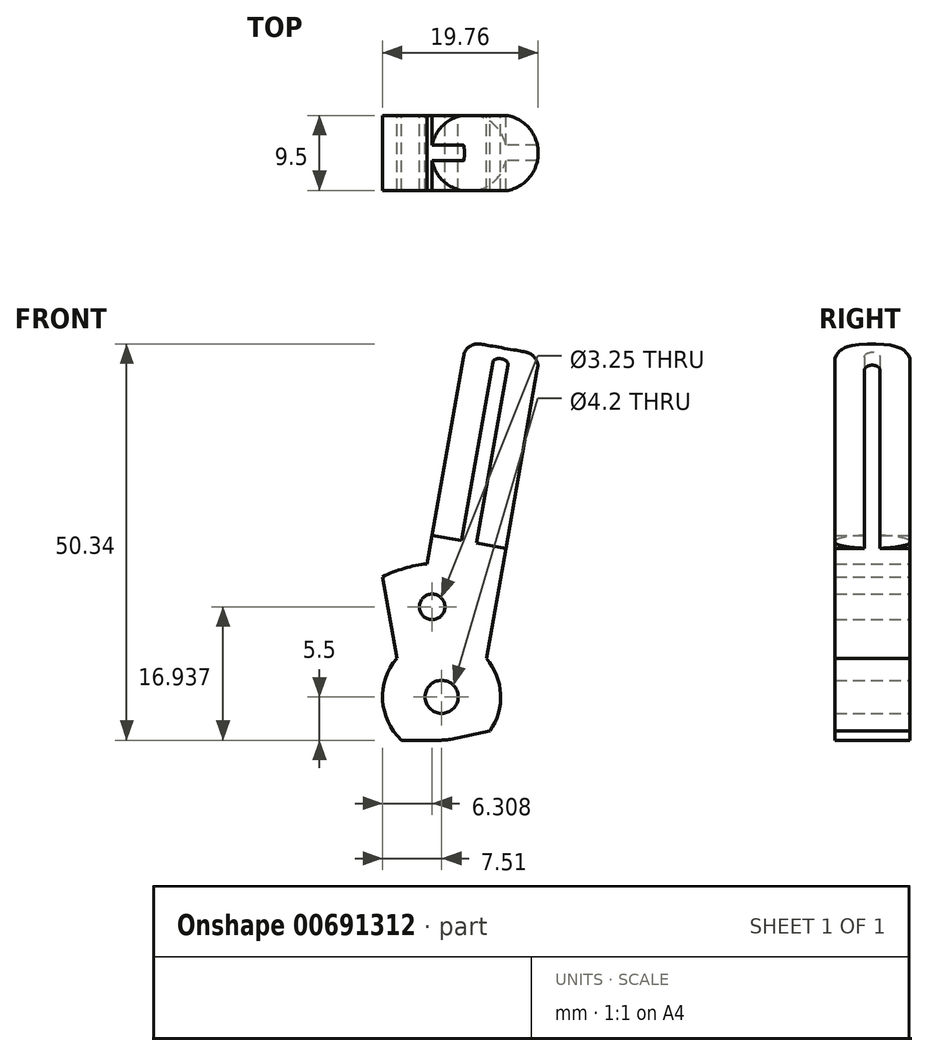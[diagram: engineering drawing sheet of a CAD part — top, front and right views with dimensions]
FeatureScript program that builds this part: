
annotation { "Feature Type Name" : "Feature", "Feature Type Description" : "" }
export const myFeature = defineFeature(function(context is Context, id is Id, definition is map)
    precondition{}
    {
        {
            var Q0;
            Q0=qCreatedBy(makeId("Front.planeOp"),FACE);
            var sketch = newSketch(context, id + "F0", { "sketchPlane" : qUnion([Q0])});
            skLineSegment(sketch, "E0.top", {"start": v(-21.4, -7.5) * mm, "end": v(21.4, -7.5) * mm});
            skLineSegment(sketch, "E0.left", {"start": v(-21.4, 17.9) * mm, "end": v(-21.4, -7.5) * mm, "construction": true});
            skLineSegment(sketch, "E0.right", {"start": v(21.4, 17.9) * mm, "end": v(21.4, -7.5) * mm});
            skCircle(sketch, "E1", {"center": v(0, 0) * mm, "radius": 2.1 * mm});
            skCircle(sketch, "E2", {"center": v(0, 0) * mm, "radius": 7.5 * mm});
            skLineSegment(sketch, "E3", {"start": v(0, 0) * mm, "end": v(13.06, 74.1) * mm, "construction": true});
            skLineSegment(sketch, "E4", {"start": v(10.99, 62.3) * mm, "end": v(6.3, 63.13) * mm});
            skLineSegment(sketch, "E5.MirrorCS", {"start": v(10.99, 62.3) * mm, "end": v(15.66, 61.48) * mm});
            skLineSegment(sketch, "E6", {"start": v(6.3, 63.13) * mm, "end": v(2, 38.7) * mm});
            skLineSegment(sketch, "E7", {"start": v(2, 38.7) * mm, "end": v(11.36, 37.05) * mm});
            skPoint(sketch, "E7.endSnap0", {"position": v(6.53, 37.05) * mm});
            skLineSegment(sketch, "E8", {"start": v(11.36, 37.05) * mm, "end": v(15.66, 61.48) * mm});
            skLineSegment(sketch, "E9", {"start": v(-66.42, 0) * mm, "end": v(-66.42, -3.81) * mm, "construction": true});
            skLineSegment(sketch, "E10", {"start": v(-49.76, -7.5) * mm, "end": v(-49.76, -3.5) * mm, "construction": true});
            skLineSegment(sketch, "E11", {"start": v(-49.76, -3.5) * mm, "end": v(40.68, -3.5) * mm, "construction": true});
            skLineSegment(sketch, "E12", {"start": v(-46.54, -7.5) * mm, "end": v(-46.54, -5.5) * mm, "construction": true});
            skLineSegment(sketch, "E13", {"start": v(-46.54, -5.5) * mm, "end": v(40.68, -5.5) * mm, "construction": true});
            skLineSegment(sketch, "E14", {"start": v(-21.4, -3.5) * mm, "end": v(21.4, -3.5) * mm});
            skLineSegment(sketch, "E15", {"start": v(0, 0) * mm, "end": v(27.45, 67.94) * mm, "construction": true});
            skLineSegment(sketch, "E16", {"start": v(0, 0) * mm, "end": v(3.52, 33.49) * mm, "construction": true});
            skLineSegment(sketch, "E17", {"start": v(0, 0) * mm, "end": v(-3.56, 33.9) * mm, "construction": true});
            skArc(sketch, "E18", {"start": v(-7.34, 8.85) * mm, "mid": v(0.93, 11.46) * mm, "end": v(8.67, 7.55) * mm, "construction": true});
            skCircle(sketch, "E19", {"center": v(-1.2, 11.44) * mm, "radius": 1.63 * mm});
            skCircle(sketch, "E20", {"center": v(-1.2, 11.44) * mm, "radius": 4 * mm, "construction": true});
            skArc(sketch, "E21", {"start": v(-9.57, 14.05) * mm, "mid": v(-1.2, 16.96) * mm, "end": v(7.5, 15.26) * mm, "construction": true});
            skLineSegment(sketch, "E22", {"start": v(0, 13.36) * mm, "end": v(-7.51, 13.36) * mm, "construction": true});
            skLineSegment(sketch, "E23", {"start": v(2, 38.7) * mm, "end": v(-1.84, 16.9) * mm, "construction": true});
            skLineSegment(sketch, "E24", {"start": v(11.36, 37.05) * mm, "end": v(7.51, 15.25) * mm, "construction": true});
            skLineSegment(sketch, "E25", {"start": v(3.47, 19.7) * mm, "end": v(8.15, 18.87) * mm, "construction": true});
            skLineSegment(sketch, "E26", {"start": v(8.15, 18.87) * mm, "end": v(-1.2, 20.52) * mm});
            skLineSegment(sketch, "E27", {"start": v(-1.2, 20.52) * mm, "end": v(-1.84, 16.9) * mm});
            skLineSegment(sketch, "E28", {"start": v(8.15, 18.87) * mm, "end": v(7.51, 15.25) * mm});
            skArc(sketch, "E29", {"start": v(-7.51, 15.25) * mm, "mid": v(-4.72, 16.33) * mm, "end": v(-1.78, 16.9) * mm});
            skLineSegment(sketch, "E30", {"start": v(0, 0) * mm, "end": v(53.18, -11.3) * mm, "construction": true});
            skLineSegment(sketch, "E31", {"start": v(7.51, 15.25) * mm, "end": v(5.69, 4.9) * mm});
            skLineSegment(sketch, "E32", {"start": v(0, 0) * mm, "end": v(5.69, 4.9) * mm, "construction": true});
            skLineSegment(sketch, "E33", {"start": v(0, 0) * mm, "end": v(30.44, 16.67) * mm, "construction": true});
            skLineSegment(sketch, "E34", {"start": v(-5.1, -5.5) * mm, "end": v(0, -5.5) * mm});
            skLineSegment(sketch, "E35", {"start": v(0, 0) * mm, "end": v(5.1, -5.5) * mm, "construction": true});
            skLineSegment(sketch, "E36", {"start": v(0, 0) * mm, "end": v(15.5, -10.92) * mm, "construction": true});
            skLineSegment(sketch, "E37.MirrorCS", {"start": v(0, 0) * mm, "end": v(-5.69, 4.9) * mm, "construction": true});
            skLineSegment(sketch, "E38", {"start": v(-7.51, 15.25) * mm, "end": v(-5.69, 4.9) * mm});
            skLineSegment(sketch, "E39", {"start": v(11.36, 37.05) * mm, "end": v(5.69, 4.9) * mm});
            skLineSegment(sketch, "E40", {"start": v(0, 0) * mm, "end": v(1.85, -8.7) * mm, "construction": true});
            skArc(sketch, "E41", {"start": v(0, -5.5) * mm, "mid": v(0.57, -5.47) * mm, "end": v(1.14, -5.38) * mm});
            skLineSegment(sketch, "E42", {"start": v(1.14, -5.38) * mm, "end": v(6.13, -4.32) * mm});
            skSolve(sketch);
        }
        {
            var Q0;
            {var subQ5=sQuery(id+"F0.wireOp",EDGE,"E26");Q0=makeQuery(id+"F0.imprint","IMPRINT",FACE,{"disambiguationData":[TD([[makeQuery(id+"F0.imprint","IMPRINT",EDGE,{"derivedFrom":subQ5}),1.0]])]});}
            var Q1;
            {var subQ8=sQuery(id+"F0.wireOp",EDGE,"dcc9mgXF-Am9R-e9oT-sTfc-VprgwdTA8qZ0");Q1=makeQuery(id+"F0.imprint","IMPRINT",FACE,{"disambiguationData":[TD([[makeQuery(id+"F0.imprint","IMPRINT",EDGE,{"derivedFrom":subQ8}),1.0]])]});}
            var Q2;
            Q2=makeQuery(id+"F0.imprint","IMPRINT",FACE,{"disambiguationData":[TD([[makeQuery(id+"F0.imprint","IMPRINT",EDGE,{"derivedFrom":sQuery(id+"F0.wireOp",EDGE,"E1")}),-1.0]])]});
            var Q3;
            {var subQ0=sQuery(id+"F0.wireOp",EDGE,"E34");Q3=makeQuery(id+"F0.imprint","IMPRINT",FACE,{"disambiguationData":[TD([[makeQuery(id+"F0.imprint","IMPRINT",EDGE,{"derivedFrom":subQ0}),1.0]])]});}
            extrude(context, id + "F1", {"entities" : qUnion([Q0, Q1, Q2, Q3]), "depth" : 9.5 * mm, "offsetDistance" : 25 * mm});
        }
        {
            var Q0;
            Q0=makeQuery(id+"F1.opExtrude","SWEPT_FACE",FACE,{"disambiguationData":[OSD([sQuery(id+"F0.wireOp",EDGE,"E26")])]});
            var sketch = newSketch(context, id + "F2", { "sketchPlane" : qUnion([Q0])});
            skLineSegment(sketch, "E43", {"start": v(0, 0) * mm, "end": v(0, -9.5) * mm, "construction": true});
            skLineSegment(sketch, "E44", {"start": v(-4.75, -4.75) * mm, "end": v(4.75, -4.75) * mm, "construction": true});
            skCircle(sketch, "E45", {"center": v(0, -4.75) * mm, "radius": 4.85 * mm});
            skSolve(sketch);
        }
        {
            var Q0;
            {var subQ0=sQuery(id+"F2.wireOp",EDGE,"E45");var subQ1=sQuery(id+"F0.wireOp",EDGE,"E26");var subQ9=makeQuery(id+"F1.opExtrude","CAP_EDGE",EDGE,{"disambiguationData":[OSD([subQ1])],"isStart":true});var subQ12=makeQuery(id+"F2.imprint","INTERSECT",VERTEX,{"disambiguationData":[OD(0.0)],"derivedFrom":[subQ9,subQ0]});Q0=makeQuery(id+"F2.imprint","IMPRINT",FACE,{"disambiguationData":[TD([[makeQuery(id+"F2.imprint","IMPRINT",EDGE,{"disambiguationData":[TD([[subQ12,-1.0]])],"derivedFrom":subQ9}),1.0]])]});}
            extrude(context, id + "F3", {"entities" : qUnion([Q0]), "operationType" : NewBodyOperationType.ADD, "depth" : 25 * mm, "offsetDistance" : 25 * mm});
        }
        {
            var Q0;
            {var subQ0=sQuery(id+"F2.wireOp",EDGE,"E45");var subQ1=sQuery(id+"F0.wireOp",EDGE,"E26");Q0=makeQuery(id+"F3.opExtrude","CAP_EDGE",EDGE,{"disambiguationData":[OSD([subQ0]),TDD([makeQuery(id+"F2.imprint","IMPRINT",EDGE,{"disambiguationData":[TD([[makeQuery(id+"F2.imprint","INTERSECT",VERTEX,{"disambiguationData":[OD(0.0)],"derivedFrom":[makeQuery(id+"F1.opExtrude","CAP_EDGE",EDGE,{"disambiguationData":[OSD([subQ1])],"isStart":false}),subQ0]}),1.0]])],"derivedFrom":subQ0})])],"isStart":false});}
            fillet(context, id + "F4", {"entities" : qUnion([Q0]), "radius" : 2 * mm, "tangentPropagation" : true, "allowEdgeOverflow" : false});
        }
    });
